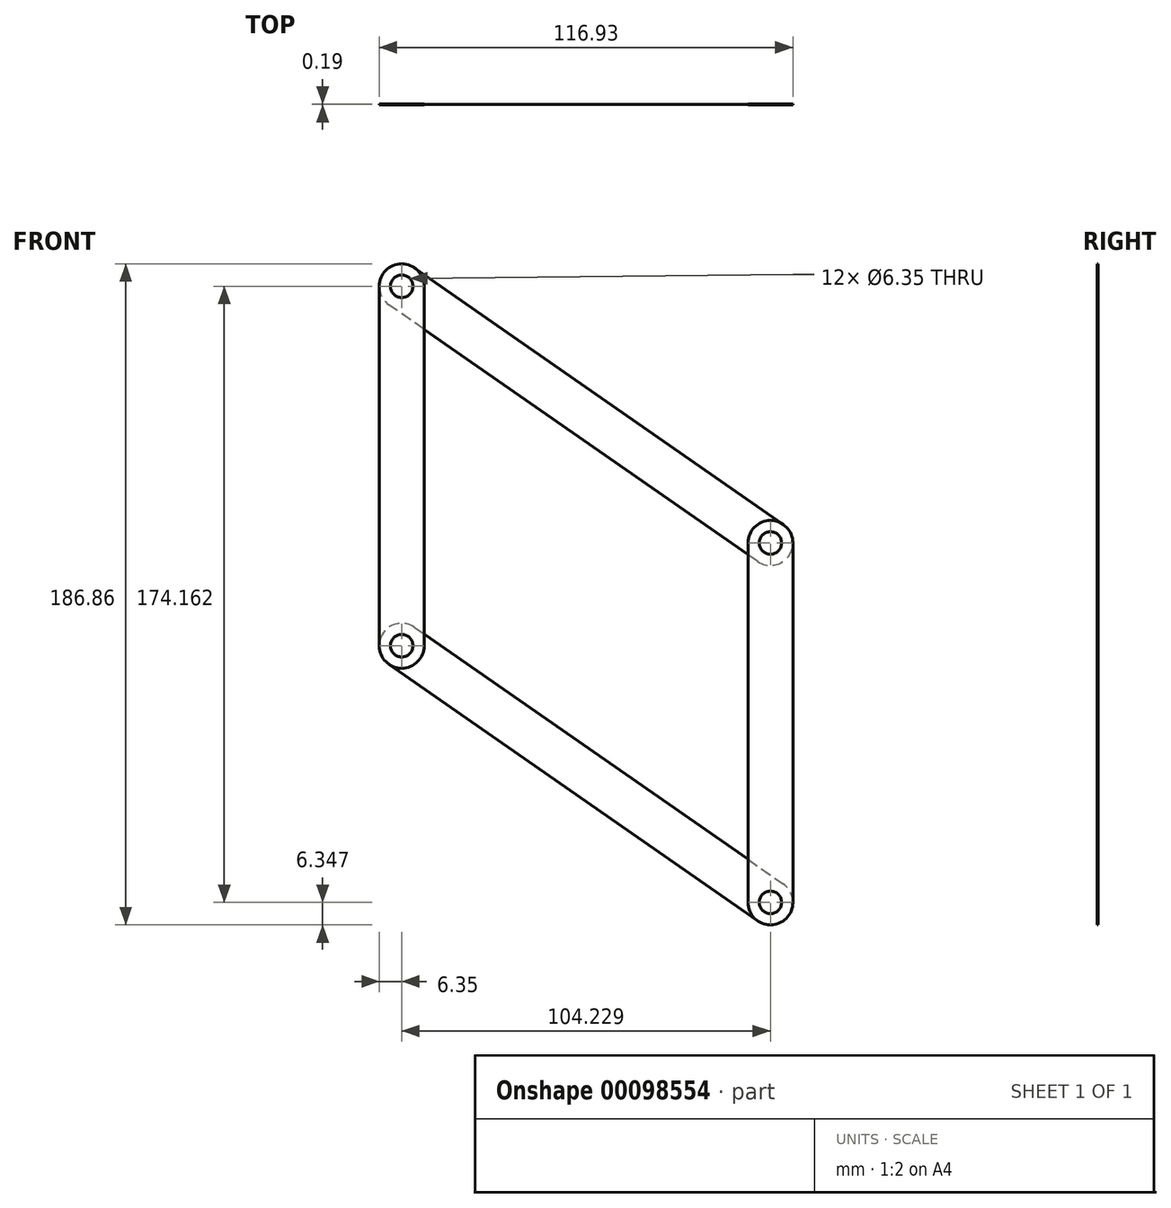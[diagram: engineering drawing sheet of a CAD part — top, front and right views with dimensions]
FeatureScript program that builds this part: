
annotation { "Feature Type Name" : "Feature", "Feature Type Description" : "" }
export const myFeature = defineFeature(function(context is Context, id is Id, definition is map)
    precondition{}
    {
        {
            assignVariable(context, id + "F0", {"name" : "LINK_THICKNESS", "anyValue" : 1 / 16});
        }
        {
            var Q0;
            Q0=qCreatedBy(makeId("Front.planeOp"),FACE);
            var sketch = newSketch(context, id + "F1", { "sketchPlane" : qUnion([Q0])});
            skLineSegment(sketch, "E0", {"start": v(0, 0) * mm, "end": v(104.23, -72.56) * mm});
            skLineSegment(sketch, "E1", {"start": v(104.23, -72.56) * mm, "end": v(104.23, 29.04) * mm});
            skLineSegment(sketch, "E2", {"start": v(104.23, 29.04) * mm, "end": v(0, 101.6) * mm});
            skLineSegment(sketch, "E3", {"start": v(0, 101.6) * mm, "end": v(0, 0) * mm});
            skPoint(sketch, "E4.middle", {"position": v(0, 50.8) * mm});
            skSolve(sketch);
        }
        {
            var Q0;
            Q0=qCreatedBy(makeId("Front.planeOp"),FACE);
            var sketch = newSketch(context, id + "F2", { "sketchPlane" : qUnion([Q0])});
            skLineSegment(sketch, "E5.0", {"start": v(0, 101.6) * mm, "end": v(0, 0) * mm, "construction": true});
            skLineSegment(sketch, "E6.bottom", {"start": v(6.35, 101.6) * mm, "end": v(-6.35, 101.6) * mm, "construction": true});
            skLineSegment(sketch, "E6.top", {"start": v(6.35, 0) * mm, "end": v(-6.35, 0) * mm, "construction": true});
            skLineSegment(sketch, "E6.left", {"start": v(6.35, 101.6) * mm, "end": v(6.35, 0) * mm});
            skLineSegment(sketch, "E6.right", {"start": v(-6.35, 101.6) * mm, "end": v(-6.35, 0) * mm});
            skPoint(sketch, "E6.middle", {"position": v(0, 50.8) * mm});
            skArc(sketch, "E7", {"start": v(-6.35, 101.6) * mm, "mid": v(0, 107.95) * mm, "end": v(6.35, 101.6) * mm});
            skArc(sketch, "E8", {"start": v(6.35, 0) * mm, "mid": v(0, -6.35) * mm, "end": v(-6.35, 0) * mm});
            skCircle(sketch, "E9", {"center": v(0, 101.6) * mm, "radius": 3.18 * mm});
            skCircle(sketch, "E10", {"center": v(0, 0) * mm, "radius": 3.18 * mm});
            skSolve(sketch);
        }
        {
            var Q0;
            Q0=makeQuery(id+"F2.imprint","IMPRINT",FACE,{"disambiguationData":[TD([[makeQuery(id+"F2.imprint","IMPRINT",EDGE,{"derivedFrom":sQuery(id+"F2.wireOp",EDGE,"E6.left")}),-1.0]])]});
            extrude(context, id + "F3", {"entities" : qUnion([Q0]), "depth" : (getVariable(context, 'LINK_THICKNESS')) * mm});
        }
        {
            var Q0;
            Q0=qCreatedBy(makeId("Front.planeOp"),FACE);
            var sketch = newSketch(context, id + "F4", { "sketchPlane" : qUnion([Q0])});
            skLineSegment(sketch, "E11.0", {"start": v(104.23, 29.04) * mm, "end": v(0, 101.6) * mm, "construction": true});
            skArc(sketch, "E12", {"start": v(3.63, 106.81) * mm, "mid": v(-5.21, 105.23) * mm, "end": v(-3.63, 96.39) * mm});
            skArc(sketch, "E13", {"start": v(100.6, 23.83) * mm, "mid": v(109.44, 25.4) * mm, "end": v(107.86, 34.25) * mm});
            skLineSegment(sketch, "E14", {"start": v(3.63, 106.81) * mm, "end": v(107.86, 34.25) * mm});
            skLineSegment(sketch, "E15", {"start": v(100.6, 23.83) * mm, "end": v(-3.63, 96.39) * mm});
            skCircle(sketch, "E16", {"center": v(0, 101.6) * mm, "radius": 3.18 * mm});
            skCircle(sketch, "E17", {"center": v(104.23, 29.04) * mm, "radius": 3.18 * mm});
            skSolve(sketch);
        }
        {
            var Q0;
            Q0=makeQuery(id+"F4.imprint","IMPRINT",FACE,{"disambiguationData":[TD([[makeQuery(id+"F4.imprint","IMPRINT",EDGE,{"derivedFrom":sQuery(id+"F4.wireOp",EDGE,"E12")}),1.0]])]});
            extrude(context, id + "F5", {"entities" : qUnion([Q0]), "oppositeDirection" : true, "depth" : (getVariable(context, 'LINK_THICKNESS')) * mm});
        }
        {
            var Q0;
            Q0=makeQuery(id+"F5.opExtrude","SWEPT_BODY",BODY,{"disambiguationData":[OSD([sQuery(id+"F4.wireOp",EDGE,"E12"),sQuery(id+"F4.wireOp",EDGE,"E13"),sQuery(id+"F4.wireOp",EDGE,"E14"),sQuery(id+"F4.wireOp",EDGE,"E15"),sQuery(id+"F4.wireOp",EDGE,"E16"),sQuery(id+"F4.wireOp",EDGE,"E17")])]});
            var Q1;
            Q1=sQuery(id+"F1.wireOp",EDGE,"E3");
            transform(context, id + "F6", {"entities" : qUnion([Q0]), "transformType" : TransformType.TRANSLATION_ENTITY, "oppositeDirectionEntity" : false, "transformLine" : qUnion([Q1]), "makeCopy" : true});
        }
        {
            var Q0;
            Q0=makeQuery(id+"F3.opExtrude","SWEPT_BODY",BODY,{"disambiguationData":[OSD([sQuery(id+"F2.wireOp",EDGE,"E6.left"),sQuery(id+"F2.wireOp",EDGE,"E6.right"),sQuery(id+"F2.wireOp",EDGE,"E7"),sQuery(id+"F2.wireOp",EDGE,"E8"),sQuery(id+"F2.wireOp",EDGE,"E9"),sQuery(id+"F2.wireOp",EDGE,"E10")])]});
            var Q1;
            Q1=sQuery(id+"F1.wireOp",EDGE,"E2");
            transform(context, id + "F7", {"entities" : qUnion([Q0]), "transformType" : TransformType.TRANSLATION_ENTITY, "oppositeDirectionEntity" : true, "transformLine" : qUnion([Q1]), "makeCopy" : true});
        }
        {
            var Q0;
            Q0=makeQuery(id+"F3.opExtrude","SWEPT_BODY",BODY,{"disambiguationData":[OSD([sQuery(id+"F2.wireOp",EDGE,"E6.left"),sQuery(id+"F2.wireOp",EDGE,"E6.right"),sQuery(id+"F2.wireOp",EDGE,"E7"),sQuery(id+"F2.wireOp",EDGE,"E8"),sQuery(id+"F2.wireOp",EDGE,"E9"),sQuery(id+"F2.wireOp",EDGE,"E10")])]});
            var Q1;
            Q1=makeQuery(id+"F7.opPattern","COPY",BODY,{"derivedFrom":makeQuery(id+"F3.opExtrude","SWEPT_BODY",BODY,{"disambiguationData":[OSD([sQuery(id+"F2.wireOp",EDGE,"E6.left"),sQuery(id+"F2.wireOp",EDGE,"E6.right"),sQuery(id+"F2.wireOp",EDGE,"E7"),sQuery(id+"F2.wireOp",EDGE,"E8"),sQuery(id+"F2.wireOp",EDGE,"E9"),sQuery(id+"F2.wireOp",EDGE,"E10")])]}),"instanceName":"1"});
            transform(context, id + "F8", {"entities" : qUnion([Q0, Q1]), "transformType" : TransformType.TRANSLATION_3D, "dx" : 0 * mm, "dy" : 2 * (getVariable(context, 'LINK_THICKNESS')) * mm, "dz" : 0 * mm, "makeCopy" : true});
        }
    });
